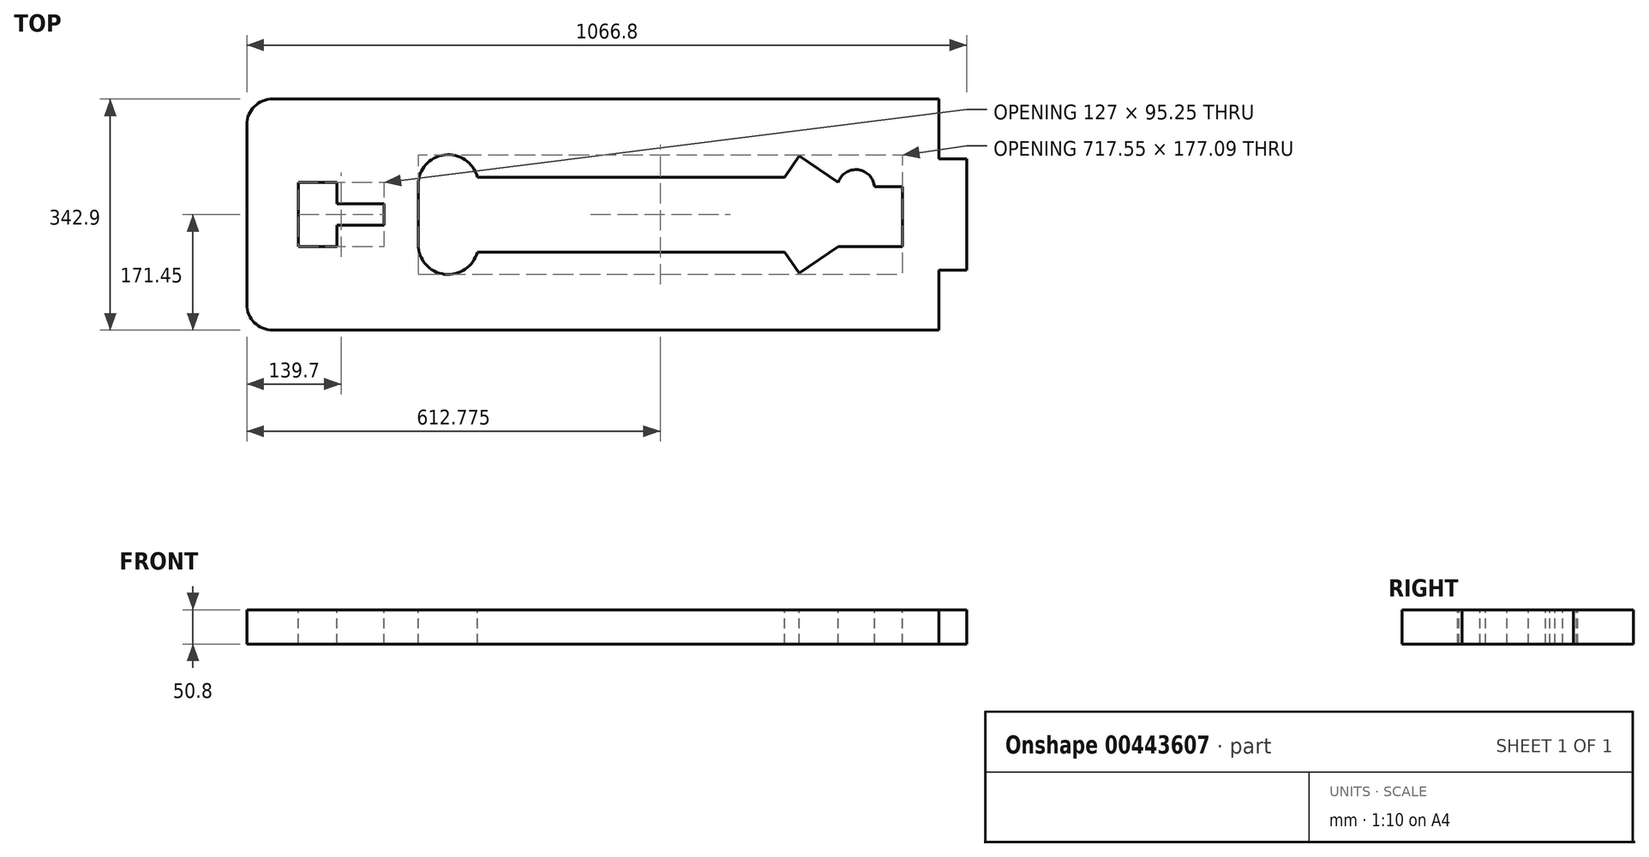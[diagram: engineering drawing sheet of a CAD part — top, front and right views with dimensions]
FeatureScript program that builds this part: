
annotation { "Feature Type Name" : "Feature", "Feature Type Description" : "" }
export const myFeature = defineFeature(function(context is Context, id is Id, definition is map)
    precondition{}
    {
        {
            var Q0;
            Q0=qCreatedBy(makeId("Top.planeOp"),FACE);
            var sketch = newSketch(context, id + "F0", { "sketchPlane" : qUnion([Q0])});
            skLineSegment(sketch, "E0.bottom", {"start": v(533.4, -171.45) * mm, "end": v(-533.4, -171.45) * mm});
            skLineSegment(sketch, "E0.top", {"start": v(533.4, 171.45) * mm, "end": v(-533.4, 171.45) * mm});
            skLineSegment(sketch, "E0.left", {"start": v(533.4, -171.45) * mm, "end": v(533.4, 171.45) * mm});
            skLineSegment(sketch, "E0.right", {"start": v(-533.4, -171.45) * mm, "end": v(-533.4, 171.45) * mm});
            skPoint(sketch, "E0.middle", {"position": v(0, 0) * mm});
            skSolve(sketch);
        }
        {
            var Q0;
            Q0=qSketchRegion(id+"F0",true);
            extrude(context, id + "F1", {"entities" : qUnion([Q0]), "depth" : 50.8 * mm});
        }
        {
            var Q0;
            Q0=makeQuery(id+"F1.opExtrude","SWEPT_EDGE",EDGE,{"disambiguationData":[OSD([sQuery(id+"F0.wireOp",EDGE,"E0.top"),sQuery(id+"F0.wireOp",EDGE,"E0.right")])]});
            var Q1;
            Q1=makeQuery(id+"F1.opExtrude","SWEPT_EDGE",EDGE,{"disambiguationData":[OSD([sQuery(id+"F0.wireOp",EDGE,"E0.bottom"),sQuery(id+"F0.wireOp",EDGE,"E0.right")])]});
            var Q2;
            Q2=makeQuery(id+"F1.opExtrude","SWEPT_EDGE",EDGE,{"disambiguationData":[OSD([sQuery(id+"F0.wireOp",EDGE,"E0.top"),sQuery(id+"F0.wireOp",EDGE,"E0.left")])]});
            var Q3;
            Q3=makeQuery(id+"F1.opExtrude","SWEPT_EDGE",EDGE,{"disambiguationData":[OSD([sQuery(id+"F0.wireOp",EDGE,"E0.bottom"),sQuery(id+"F0.wireOp",EDGE,"E0.left")])]});
            fillet(context, id + "F2", {"entities" : qUnion([Q0, Q1, Q2, Q3]), "radius" : 38.1 * mm, "tangentPropagation" : true, "allowEdgeOverflow" : false});
        }
        {
            var Q0;
            Q0=makeQuery(id+"F1.opExtrude","CAP_FACE",FACE,{"disambiguationData":[OSD([sQuery(id+"F0.wireOp",EDGE,"E0.bottom"),sQuery(id+"F0.wireOp",EDGE,"E0.top"),sQuery(id+"F0.wireOp",EDGE,"E0.left"),sQuery(id+"F0.wireOp",EDGE,"E0.right")])],"isStart":false});
            var sketch = newSketch(context, id + "F3", { "sketchPlane" : qUnion([Q0])});
            skLineSegment(sketch, "E1", {"start": v(492.13, 171.45) * mm, "end": v(492.13, 82.55) * mm});
            skLineSegment(sketch, "E2", {"start": v(492.13, 82.55) * mm, "end": v(533.4, 82.55) * mm});
            skLineSegment(sketch, "E3", {"start": v(492.13, -171.45) * mm, "end": v(492.13, -82.55) * mm});
            skLineSegment(sketch, "E4", {"start": v(492.13, -82.55) * mm, "end": v(533.4, -82.55) * mm});
            skLineSegment(sketch, "E5", {"start": v(533.4, -82.55) * mm, "end": v(533.4, -171.45) * mm});
            skLineSegment(sketch, "E6", {"start": v(533.4, -171.45) * mm, "end": v(492.13, -171.45) * mm});
            skLineSegment(sketch, "E7", {"start": v(492.13, 171.45) * mm, "end": v(533.4, 171.45) * mm});
            skLineSegment(sketch, "E8", {"start": v(533.4, 171.45) * mm, "end": v(533.4, 82.55) * mm});
            skSolve(sketch);
        }
        {
            var Q0;
            Q0 = qSketchRegion(id + "F3", true);
            extrude(context, id + "F4", {"entities" : qUnion([Q0]), "operationType" : NewBodyOperationType.REMOVE, "oppositeDirection" : true, "depth" : 50.8 * mm});
        }
        {
            var Q0;
            Q0=makeQuery(id+"F1.opExtrude","CAP_FACE",FACE,{"disambiguationData":[OSD([sQuery(id+"F0.wireOp",EDGE,"E0.bottom"),sQuery(id+"F0.wireOp",EDGE,"E0.top"),sQuery(id+"F0.wireOp",EDGE,"E0.left"),sQuery(id+"F0.wireOp",EDGE,"E0.right")])],"isStart":false});
            var sketch = newSketch(context, id + "F5", { "sketchPlane" : qUnion([Q0])});
            skLineSegment(sketch, "E9", {"start": v(-457.2, 47.62) * mm, "end": v(-457.2, -47.62) * mm});
            skLineSegment(sketch, "E10", {"start": v(-457.2, -47.63) * mm, "end": v(-400.05, -47.63) * mm});
            skLineSegment(sketch, "E11", {"start": v(-400.05, -47.63) * mm, "end": v(-400.05, -15.88) * mm});
            skLineSegment(sketch, "E12", {"start": v(-400.05, -15.88) * mm, "end": v(-330.2, -15.88) * mm});
            skLineSegment(sketch, "E13", {"start": v(-330.2, -15.88) * mm, "end": v(-330.2, 15.88) * mm});
            skLineSegment(sketch, "E14", {"start": v(-330.2, 15.88) * mm, "end": v(-400.05, 15.88) * mm});
            skLineSegment(sketch, "E15", {"start": v(-400.05, 15.88) * mm, "end": v(-400.05, 47.63) * mm});
            skLineSegment(sketch, "E16", {"start": v(-400.05, 47.63) * mm, "end": v(-457.2, 47.62) * mm});
            skSolve(sketch);
        }
        {
            var Q0;
            Q0=makeQuery(id+"F5.imprint","IMPRINT",FACE,{"disambiguationData":[TD([[makeQuery(id+"F5.imprint","IMPRINT",EDGE,{"derivedFrom":sQuery(id+"F5.wireOp",EDGE,"E9")}),-1.0]])]});
            var sketch = newSketch(context, id + "F6", { "sketchPlane" : qUnion([Q0])});
            skCircle(sketch, "E17", {"center": v(-234.95, 44.45) * mm, "radius": 44.45 * mm});
            skCircle(sketch, "E18", {"center": v(-234.95, -44.45) * mm, "radius": 44.45 * mm});
            skLineSegment(sketch, "E19", {"start": v(-191.91, 55.56) * mm, "end": v(263.73, 55.56) * mm});
            skLineSegment(sketch, "E20", {"start": v(263.73, 55.56) * mm, "end": v(285.22, 87.02) * mm});
            skLineSegment(sketch, "E21", {"start": v(396.87, 41.27) * mm, "end": v(438.15, 41.27) * mm});
            skLineSegment(sketch, "E22", {"start": v(342.9, -47.63) * mm, "end": v(285.22, -87.02) * mm});
            skLineSegment(sketch, "E23", {"start": v(285.22, 87.02) * mm, "end": v(342.9, 47.62) * mm});
            skLineSegment(sketch, "E24", {"start": v(-191.91, -55.56) * mm, "end": v(263.73, -55.56) * mm});
            skLineSegment(sketch, "E25", {"start": v(-279.4, 44.45) * mm, "end": v(-279.4, -44.45) * mm});
            skLineSegment(sketch, "E26", {"start": v(263.73, -55.56) * mm, "end": v(285.22, -87.02) * mm});
            skLineSegment(sketch, "E27", {"start": v(342.9, -47.63) * mm, "end": v(438.15, -47.63) * mm});
            skLineSegment(sketch, "E28", {"start": v(438.15, -47.63) * mm, "end": v(438.15, 41.27) * mm});
            skArc(sketch, "E29", {"start": v(396.87, 41.27) * mm, "mid": v(372.48, 66.49) * mm, "end": v(342.9, 47.62) * mm});
            skSolve(sketch);
        }
        {
            var Q0;
            Q0 = qSketchRegion(id + "F6", true);
            extrude(context, id + "F7", {"entities" : qUnion([Q0]), "operationType" : NewBodyOperationType.REMOVE, "oppositeDirection" : true, "depth" : 50.8 * mm});
        }
        {
            var Q0;
            Q0 = qSketchRegion(id + "F5", true);
            extrude(context, id + "F8", {"entities" : qUnion([Q0]), "operationType" : NewBodyOperationType.REMOVE, "oppositeDirection" : true, "depth" : 50.8 * mm});
        }
    });
